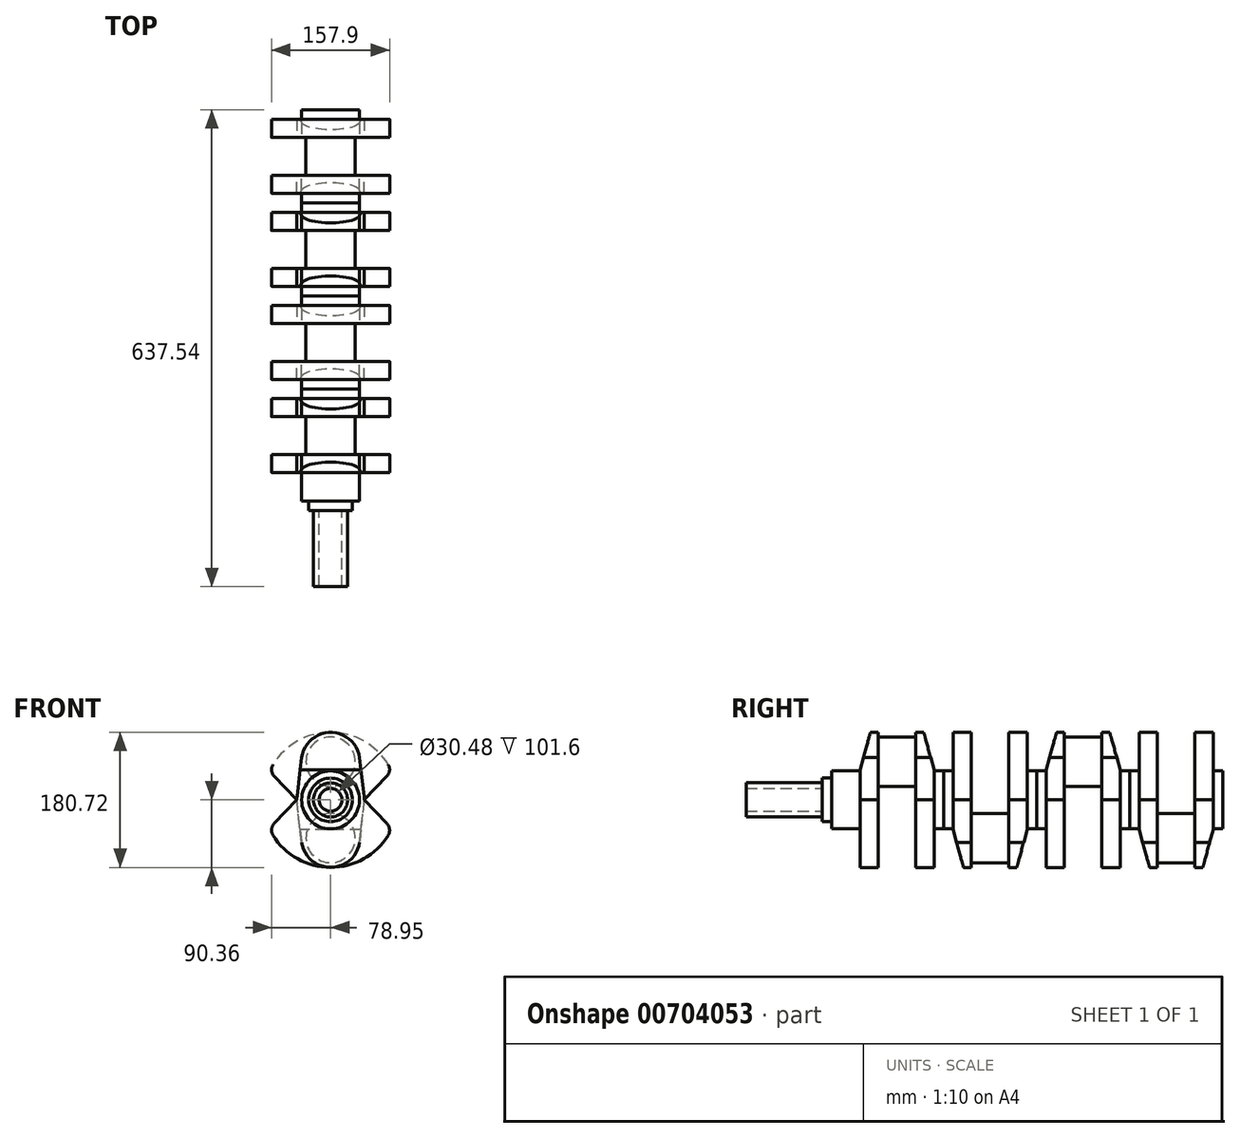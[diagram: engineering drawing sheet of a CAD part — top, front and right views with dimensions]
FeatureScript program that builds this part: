
annotation { "Feature Type Name" : "Feature", "Feature Type Description" : "" }
export const myFeature = defineFeature(function(context is Context, id is Id, definition is map)
    precondition{}
    {
        {
            var Q0;
            Q0=qCreatedBy(makeId("Front.planeOp"),FACE);
            var sketch = newSketch(context, id + "F0", { "sketchPlane" : qUnion([Q0])});
            skArc(sketch, "E0.0", {"start": v(-44.79, 5.17) * mm, "mid": v(-45.01, 2.59) * mm, "end": v(-45.09, 0) * mm});
            skLineSegment(sketch, "E1", {"start": v(-38.83, 56.77) * mm, "end": v(-44.79, 5.17) * mm});
            skLineSegment(sketch, "E2.MirrorCS", {"start": v(38.83, 56.77) * mm, "end": v(44.79, 5.17) * mm});
            skArc(sketch, "E3.trimOffspring", {"start": v(38.83, 56.77) * mm, "mid": v(0, 90.36) * mm, "end": v(-38.83, 56.77) * mm});
            skLineSegment(sketch, "E4", {"start": v(-45.09, 0) * mm, "end": v(-75.43, -31.75) * mm});
            skLineSegment(sketch, "E5.MirrorCS", {"start": v(45.09, 0) * mm, "end": v(75.43, -31.75) * mm});
            skArc(sketch, "E6", {"start": v(-77.08, -47.15) * mm, "mid": v(0, -90.36) * mm, "end": v(77.08, -47.15) * mm});
            skPoint(sketch, "E7.visualSharp", {"position": v(-81.8, -38.4) * mm});
            skArc(sketch, "E7.filletArc", {"start": v(-75.43, -31.75) * mm, "mid": v(-78.88, -39.17) * mm, "end": v(-77.08, -47.15) * mm});
            skPoint(sketch, "E8.visualSharp", {"position": v(81.8, -38.4) * mm});
            skArc(sketch, "E8.filletArc", {"start": v(77.08, -47.15) * mm, "mid": v(78.88, -39.17) * mm, "end": v(75.43, -31.75) * mm});
            skArc(sketch, "E9.trimOffspring", {"start": v(45.09, 0) * mm, "mid": v(45.01, 2.59) * mm, "end": v(44.79, 5.17) * mm});
            skSolve(sketch);
        }
        {
            var Q0;
            Q0=makeQuery(id+"F0.imprint","IMPRINT",FACE,{"disambiguationData":[TD([[makeQuery(id+"F0.imprint","IMPRINT",EDGE,{"derivedFrom":sQuery(id+"F0.wireOp",EDGE,"E0.0")}),1.0]])]});
            extrude(context, id + "F1", {"entities" : qUnion([Q0]), "depth" : 24.36 * mm, "offsetDistance" : 25.4 * mm});
        }
        {
            var Q0;
            Q0=makeQuery(id+"F1.opExtrude","CAP_FACE",FACE,{"disambiguationData":[OSD([sQuery(id+"F0.wireOp",EDGE,"E0.0"),sQuery(id+"F0.wireOp",EDGE,"E1"),sQuery(id+"F0.wireOp",EDGE,"E2.MirrorCS"),sQuery(id+"F0.wireOp",EDGE,"E3.trimOffspring"),sQuery(id+"F0.wireOp",EDGE,"E4"),sQuery(id+"F0.wireOp",EDGE,"E5.MirrorCS"),sQuery(id+"F0.wireOp",EDGE,"E6"),sQuery(id+"F0.wireOp",EDGE,"E7.filletArc"),sQuery(id+"F0.wireOp",EDGE,"E8.filletArc"),sQuery(id+"F0.wireOp",EDGE,"E9.trimOffspring")])],"isStart":false});
            var sketch = newSketch(context, id + "F2", { "sketchPlane" : qUnion([Q0])});
            skCircle(sketch, "E10", {"center": v(0, 0) * mm, "radius": 38.73 * mm});
            skSolve(sketch);
        }
        {
            var Q0;
            Q0=makeQuery(id+"F2.imprint","IMPRINT",FACE,{"disambiguationData":[TD([[makeQuery(id+"F2.imprint","IMPRINT",EDGE,{"derivedFrom":sQuery(id+"F2.wireOp",EDGE,"E10")}),1.0]])]});
            extrude(context, id + "F3", {"entities" : qUnion([Q0]), "operationType" : NewBodyOperationType.ADD, "depth" : 12.7 * mm, "offsetDistance" : 25.4 * mm});
        }
        {
            var Q0;
            Q0=makeQuery(id+"F1.opExtrude","CAP_FACE",FACE,{"disambiguationData":[OSD([sQuery(id+"F0.wireOp",EDGE,"E0.0"),sQuery(id+"F0.wireOp",EDGE,"E1"),sQuery(id+"F0.wireOp",EDGE,"E2.MirrorCS"),sQuery(id+"F0.wireOp",EDGE,"E3.trimOffspring"),sQuery(id+"F0.wireOp",EDGE,"E4"),sQuery(id+"F0.wireOp",EDGE,"E5.MirrorCS"),sQuery(id+"F0.wireOp",EDGE,"E6"),sQuery(id+"F0.wireOp",EDGE,"E7.filletArc"),sQuery(id+"F0.wireOp",EDGE,"E8.filletArc"),sQuery(id+"F0.wireOp",EDGE,"E9.trimOffspring")])],"isStart":true});
            var sketch = newSketch(context, id + "F4", { "sketchPlane" : qUnion([Q0])});
            skCircle(sketch, "E11", {"center": v(0, 51.12) * mm, "radius": 32.9 * mm});
            skSolve(sketch);
        }
        {
            var Q0;
            Q0=makeQuery(id+"F4.imprint","IMPRINT",FACE,{"disambiguationData":[TD([[makeQuery(id+"F4.imprint","IMPRINT",EDGE,{"derivedFrom":sQuery(id+"F4.wireOp",EDGE,"E11")}),1.0]])]});
            extrude(context, id + "F5", {"entities" : qUnion([Q0]), "operationType" : NewBodyOperationType.ADD, "depth" : 25.17 * mm, "offsetDistance" : 25.4 * mm});
        }
        {
            var Q0;
            Q0=qCreatedBy(makeId("Right.planeOp"),FACE);
            var sketch = newSketch(context, id + "F6", { "sketchPlane" : qUnion([Q0])});
            skLineSegment(sketch, "E12", {"start": v(-37.06, 38.73) * mm, "end": v(-24.36, 38.73) * mm, "construction": true});
            skLineSegment(sketch, "E13", {"start": v(-19.28, 95.63) * mm, "end": v(-70.85, 97.9) * mm});
            skLineSegment(sketch, "E14", {"start": v(-70.85, 97.9) * mm, "end": v(-24.36, 40) * mm});
            skLineSegment(sketch, "E15", {"start": v(-24.36, 40) * mm, "end": v(-9.23, 94.84) * mm});
            skLineSegment(sketch, "E16", {"start": v(-9.23, 94.84) * mm, "end": v(-19.28, 95.63) * mm});
            skSolve(sketch);
        }
        {
            var Q0;
            Q0=makeQuery(id+"F6.imprint","IMPRINT",FACE,{"disambiguationData":[TD([[makeQuery(id+"F6.imprint","IMPRINT",EDGE,{"derivedFrom":sQuery(id+"F6.wireOp",EDGE,"E13")}),1.0]])]});
            extrude(context, id + "F7", {"entities" : qUnion([Q0]), "operationType" : NewBodyOperationType.REMOVE, "endBound" : BoundingType.SYMMETRIC, "oppositeDirection" : true, "depth" : 201.17 * mm, "offsetDistance" : 25.4 * mm});
        }
        {
            var Q0;
            Q0=makeQuery(id+"F1.opExtrude","SWEPT_BODY",BODY,{"disambiguationData":[OSD([sQuery(id+"F0.wireOp",EDGE,"E0.0"),sQuery(id+"F0.wireOp",EDGE,"E1"),sQuery(id+"F0.wireOp",EDGE,"E2.MirrorCS"),sQuery(id+"F0.wireOp",EDGE,"E3.trimOffspring"),sQuery(id+"F0.wireOp",EDGE,"E4"),sQuery(id+"F0.wireOp",EDGE,"E5.MirrorCS"),sQuery(id+"F0.wireOp",EDGE,"E6"),sQuery(id+"F0.wireOp",EDGE,"E7.filletArc"),sQuery(id+"F0.wireOp",EDGE,"E8.filletArc"),sQuery(id+"F0.wireOp",EDGE,"E9.trimOffspring")])]});
            var Q1;
            Q1=makeQuery(id+"F5.opExtrude","CAP_FACE",FACE,{"disambiguationData":[OSD([sQuery(id+"F4.wireOp",EDGE,"E11")])],"isStart":false});
            mirror(context, id + "F8", {"operationType" : NewBodyOperationType.ADD, "entities" : qUnion([Q0]), "mirrorPlane" : qUnion([Q1])});
        }
        {
            var Q0;
            Q0=makeQuery(id+"F1.opExtrude","SWEPT_BODY",BODY,{"disambiguationData":[OSD([sQuery(id+"F0.wireOp",EDGE,"E0.0"),sQuery(id+"F0.wireOp",EDGE,"E1"),sQuery(id+"F0.wireOp",EDGE,"E2.MirrorCS"),sQuery(id+"F0.wireOp",EDGE,"E3.trimOffspring"),sQuery(id+"F0.wireOp",EDGE,"E4"),sQuery(id+"F0.wireOp",EDGE,"E5.MirrorCS"),sQuery(id+"F0.wireOp",EDGE,"E6"),sQuery(id+"F0.wireOp",EDGE,"E7.filletArc"),sQuery(id+"F0.wireOp",EDGE,"E8.filletArc"),sQuery(id+"F0.wireOp",EDGE,"E9.trimOffspring")])]});
            var Q1;
            Q1=makeQuery(id+"F8.opPattern","COPY",FACE,{"derivedFrom":makeQuery(id+"F3.opExtrude","CAP_FACE",FACE,{"disambiguationData":[OSD([sQuery(id+"F2.wireOp",EDGE,"E10")])],"isStart":false}),"instanceName":"1"});
            mirror(context, id + "F9", {"entities" : qUnion([Q0]), "mirrorPlane" : qUnion([Q1])});
        }
        {
            var Q0;
            Q0=makeQuery(id+"F9.opPattern","COPY",BODY,{"derivedFrom":makeQuery(id+"F1.opExtrude","SWEPT_BODY",BODY,{"disambiguationData":[OSD([sQuery(id+"F0.wireOp",EDGE,"E0.0"),sQuery(id+"F0.wireOp",EDGE,"E1"),sQuery(id+"F0.wireOp",EDGE,"E2.MirrorCS"),sQuery(id+"F0.wireOp",EDGE,"E3.trimOffspring"),sQuery(id+"F0.wireOp",EDGE,"E4"),sQuery(id+"F0.wireOp",EDGE,"E5.MirrorCS"),sQuery(id+"F0.wireOp",EDGE,"E6"),sQuery(id+"F0.wireOp",EDGE,"E7.filletArc"),sQuery(id+"F0.wireOp",EDGE,"E8.filletArc"),sQuery(id+"F0.wireOp",EDGE,"E9.trimOffspring")])]}),"instanceName":"1"});
            var Q1;
            Q1=makeQuery(id+"F1.opExtrude","SWEPT_BODY",BODY,{"disambiguationData":[OSD([sQuery(id+"F0.wireOp",EDGE,"E0.0"),sQuery(id+"F0.wireOp",EDGE,"E1"),sQuery(id+"F0.wireOp",EDGE,"E2.MirrorCS"),sQuery(id+"F0.wireOp",EDGE,"E3.trimOffspring"),sQuery(id+"F0.wireOp",EDGE,"E4"),sQuery(id+"F0.wireOp",EDGE,"E5.MirrorCS"),sQuery(id+"F0.wireOp",EDGE,"E6"),sQuery(id+"F0.wireOp",EDGE,"E7.filletArc"),sQuery(id+"F0.wireOp",EDGE,"E8.filletArc"),sQuery(id+"F0.wireOp",EDGE,"E9.trimOffspring")])]});
            var Q2;
            Q2=makeQuery(id+"F9.opPattern","COPY",FACE,{"derivedFrom":makeQuery(id+"F3.opExtrude","CAP_FACE",FACE,{"disambiguationData":[OSD([sQuery(id+"F2.wireOp",EDGE,"E10")])],"isStart":false}),"instanceName":"1"});
            mirror(context, id + "F10", {"entities" : qUnion([Q0, Q1]), "mirrorPlane" : qUnion([Q2])});
        }
        {
            var Q0;
            Q0=makeQuery(id+"F9.opPattern","COPY",BODY,{"derivedFrom":makeQuery(id+"F1.opExtrude","SWEPT_BODY",BODY,{"disambiguationData":[OSD([sQuery(id+"F0.wireOp",EDGE,"E0.0"),sQuery(id+"F0.wireOp",EDGE,"E1"),sQuery(id+"F0.wireOp",EDGE,"E2.MirrorCS"),sQuery(id+"F0.wireOp",EDGE,"E3.trimOffspring"),sQuery(id+"F0.wireOp",EDGE,"E4"),sQuery(id+"F0.wireOp",EDGE,"E5.MirrorCS"),sQuery(id+"F0.wireOp",EDGE,"E6"),sQuery(id+"F0.wireOp",EDGE,"E7.filletArc"),sQuery(id+"F0.wireOp",EDGE,"E8.filletArc"),sQuery(id+"F0.wireOp",EDGE,"E9.trimOffspring")])]}),"instanceName":"1"});
            var Q1;
            Q1=makeQuery(id+"F3.opExtrude","CAP_EDGE",EDGE,{"disambiguationData":[OSD([sQuery(id+"F2.wireOp",EDGE,"E10")])],"isStart":false});
            transform(context, id + "F11", {"entities" : qUnion([Q0]), "transformType" : TransformType.ROTATION, "transformAxis" : qUnion([Q1]), "angle" : 180 * degree, "makeCopy" : false});
        }
        {
            var Q0;
            Q0=makeQuery(id+"F10.opPattern","COPY",BODY,{"derivedFrom":makeQuery(id+"F1.opExtrude","SWEPT_BODY",BODY,{"disambiguationData":[OSD([sQuery(id+"F0.wireOp",EDGE,"E0.0"),sQuery(id+"F0.wireOp",EDGE,"E1"),sQuery(id+"F0.wireOp",EDGE,"E2.MirrorCS"),sQuery(id+"F0.wireOp",EDGE,"E3.trimOffspring"),sQuery(id+"F0.wireOp",EDGE,"E4"),sQuery(id+"F0.wireOp",EDGE,"E5.MirrorCS"),sQuery(id+"F0.wireOp",EDGE,"E6"),sQuery(id+"F0.wireOp",EDGE,"E7.filletArc"),sQuery(id+"F0.wireOp",EDGE,"E8.filletArc"),sQuery(id+"F0.wireOp",EDGE,"E9.trimOffspring")])]}),"instanceName":"1"});
            var Q1;
            Q1=makeQuery(id+"F3.opExtrude","CAP_EDGE",EDGE,{"disambiguationData":[OSD([sQuery(id+"F2.wireOp",EDGE,"E10")])],"isStart":false});
            transform(context, id + "F12", {"entities" : qUnion([Q0]), "transformType" : TransformType.ROTATION, "transformAxis" : qUnion([Q1]), "angle" : 180 * degree, "makeCopy" : false});
        }
        {
            var Q0;
            Q0=makeQuery(id+"F3.opExtrude","CAP_FACE",FACE,{"disambiguationData":[OSD([sQuery(id+"F2.wireOp",EDGE,"E10")])],"isStart":false});
            extrude(context, id + "F13", {"entities" : qUnion([Q0]), "operationType" : NewBodyOperationType.ADD, "depth" : 25.4 * mm, "offsetDistance" : 25.4 * mm});
        }
        {
            var Q0;
            Q0=makeQuery(id+"F13.opExtrude","CAP_FACE",FACE,{"disambiguationData":[OSD([sQuery(id+"F2.wireOp",EDGE,"E10")])],"isStart":false});
            var sketch = newSketch(context, id + "F14", { "sketchPlane" : qUnion([Q0])});
            skCircle(sketch, "E17", {"center": v(0, 0) * mm, "radius": 29.21 * mm});
            skSolve(sketch);
        }
        {
            var Q0;
            Q0=makeQuery(id+"F14.imprint","IMPRINT",FACE,{"disambiguationData":[TD([[makeQuery(id+"F14.imprint","IMPRINT",EDGE,{"derivedFrom":sQuery(id+"F14.wireOp",EDGE,"E17")}),1.0]])]});
            extrude(context, id + "F15", {"entities" : qUnion([Q0]), "operationType" : NewBodyOperationType.ADD, "depth" : 12.7 * mm, "offsetDistance" : 25.4 * mm});
        }
        {
            var Q0;
            Q0=makeQuery(id+"F15.opExtrude","CAP_FACE",FACE,{"disambiguationData":[OSD([sQuery(id+"F14.wireOp",EDGE,"E17")])],"isStart":false});
            var sketch = newSketch(context, id + "F16", { "sketchPlane" : qUnion([Q0])});
            skCircle(sketch, "E18", {"center": v(0, 0) * mm, "radius": 22.86 * mm});
            skCircle(sketch, "E19.0", {"center": v(0, 0) * mm, "radius": 15.24 * mm});
            skSolve(sketch);
        }
        {
            var Q0;
            Q0=makeQuery(id+"F16.imprint","IMPRINT",FACE,{"disambiguationData":[TD([[makeQuery(id+"F16.imprint","IMPRINT",EDGE,{"derivedFrom":sQuery(id+"F16.wireOp",EDGE,"E18")}),1.0]])]});
            extrude(context, id + "F17", {"entities" : qUnion([Q0]), "operationType" : NewBodyOperationType.ADD, "depth" : 101.6 * mm, "offsetDistance" : 25.4 * mm});
        }
    });
